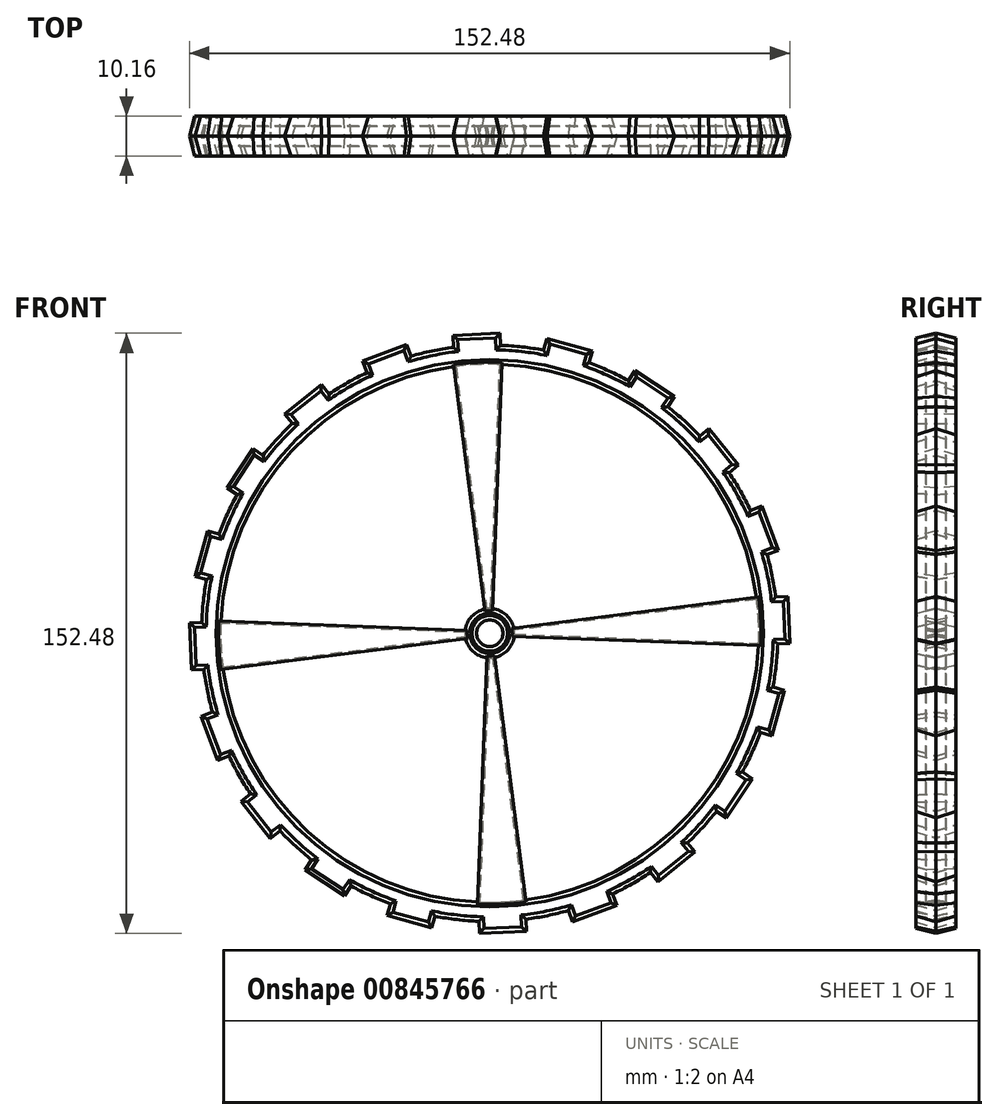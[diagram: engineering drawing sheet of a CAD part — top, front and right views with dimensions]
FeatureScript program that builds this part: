
annotation { "Feature Type Name" : "Feature", "Feature Type Description" : "" }
export const myFeature = defineFeature(function(context is Context, id is Id, definition is map)
    precondition{}
    {
        {
            var Q0;
            Q0=qCreatedBy(makeId("Front.planeOp"),FACE);
            var sketch = newSketch(context, id + "F0", { "sketchPlane" : qUnion([Q0])});
            skArc(sketch, "E0.cCircle", {"start": v(2.62, 76) * mm, "mid": v(-3.37, 75.98) * mm, "end": v(-9.34, 75.47) * mm, "construction": true});
            skLineSegment(sketch, "E0.3", {"start": v(75.71, 9.35) * mm, "end": v(76.24, -2.6) * mm});
            skLineSegment(sketch, "E0.5", {"start": v(73.3, -20.27) * mm, "end": v(71.7, -26.04) * mm});
            skLineSegment(sketch, "E0.7", {"start": v(66.75, -36.93) * mm, "end": v(60.15, -46.92) * mm});
            skLineSegment(sketch, "E0.9", {"start": v(52.07, -55.75) * mm, "end": v(47.39, -59.48) * mm});
            skLineSegment(sketch, "E0.11", {"start": v(32.3, -69.11) * mm, "end": v(21.08, -73.32) * mm});
            skLineSegment(sketch, "E0.13", {"start": v(9.35, -75.71) * mm, "end": v(-2.6, -76.24) * mm});
            skLineSegment(sketch, "E0.17", {"start": v(-36.93, -66.75) * mm, "end": v(-46.92, -60.15) * mm});
            skLineSegment(sketch, "E0.23", {"start": v(-75.71, -9.35) * mm, "end": v(-76.24, 2.6) * mm});
            skLineSegment(sketch, "E0.25", {"start": v(-74.9, 14.5) * mm, "end": v(-71.7, 26.04) * mm});
            skLineSegment(sketch, "E0.27", {"start": v(-66.75, 36.93) * mm, "end": v(-60.15, 46.92) * mm});
            skLineSegment(sketch, "E0.29", {"start": v(-52.07, 55.75) * mm, "end": v(-42.7, 63.21) * mm});
            skLineSegment(sketch, "E0.31", {"start": v(-32.3, 69.11) * mm, "end": v(-21.08, 73.32) * mm});
            skLineSegment(sketch, "E0.33", {"start": v(-9.35, 75.71) * mm, "end": v(2.6, 76.24) * mm});
            skLineSegment(sketch, "E0.35", {"start": v(14.5, 74.9) * mm, "end": v(26.04, 71.7) * mm});
            skLineSegment(sketch, "E0.37", {"start": v(36.93, 66.75) * mm, "end": v(46.92, 60.15) * mm});
            skLineSegment(sketch, "E0.39", {"start": v(55.75, 52.07) * mm, "end": v(63.21, 42.7) * mm});
            skPoint(sketch, "E0.0.midPoint", {"position": v(66.16, 37.5) * mm});
            skLineSegment(sketch, "E1", {"start": v(-9.35, 75.71) * mm, "end": v(-9.22, 72.64) * mm});
            skLineSegment(sketch, "E2", {"start": v(2.6, 76.24) * mm, "end": v(2.74, 73.17) * mm});
            skLineSegment(sketch, "E3", {"start": v(14.5, 74.9) * mm, "end": v(13.68, 71.93) * mm});
            skLineSegment(sketch, "E4", {"start": v(26.04, 71.7) * mm, "end": v(25.22, 68.74) * mm});
            skLineSegment(sketch, "E5", {"start": v(36.93, 66.75) * mm, "end": v(35.24, 64.18) * mm});
            skLineSegment(sketch, "E6", {"start": v(-36.93, -66.75) * mm, "end": v(-35.24, -64.18) * mm});
            skLineSegment(sketch, "E7", {"start": v(55.75, 52.07) * mm, "end": v(53.35, 50.15) * mm});
            skLineSegment(sketch, "E8", {"start": v(-55.75, -52.07) * mm, "end": v(-55.57, -51.92) * mm});
            skLineSegment(sketch, "E9", {"start": v(69.11, 32.3) * mm, "end": v(66.23, 31.21) * mm});
            skLineSegment(sketch, "E10", {"start": v(-69.11, -32.3) * mm, "end": v(-66.23, -31.21) * mm});
            skLineSegment(sketch, "E11", {"start": v(75.71, 9.35) * mm, "end": v(72.64, 9.22) * mm});
            skLineSegment(sketch, "E12", {"start": v(-75.71, -9.35) * mm, "end": v(-72.64, -9.22) * mm});
            skLineSegment(sketch, "E13", {"start": v(74.9, -14.5) * mm, "end": v(71.93, -13.68) * mm});
            skLineSegment(sketch, "E14", {"start": v(-74.9, 14.5) * mm, "end": v(-71.93, 13.68) * mm});
            skLineSegment(sketch, "E15", {"start": v(66.75, -36.93) * mm, "end": v(64.18, -35.24) * mm});
            skLineSegment(sketch, "E16", {"start": v(-66.75, 36.93) * mm, "end": v(-64.18, 35.24) * mm});
            skLineSegment(sketch, "E17", {"start": v(52.1, -55.6) * mm, "end": v(50.24, -53.27) * mm});
            skLineSegment(sketch, "E18", {"start": v(-52.07, 55.75) * mm, "end": v(-50.15, 53.35) * mm});
            skLineSegment(sketch, "E19", {"start": v(32.3, -69.11) * mm, "end": v(31.21, -66.23) * mm});
            skLineSegment(sketch, "E20", {"start": v(-32.3, 69.11) * mm, "end": v(-31.21, 66.23) * mm});
            skArc(sketch, "E21.trimOffspring", {"start": v(25.98, 71.48) * mm, "mid": v(20.27, 73.3) * mm, "end": v(14.44, 74.67) * mm, "construction": true});
            skArc(sketch, "E22.trimOffspring", {"start": v(46.8, 59.95) * mm, "mid": v(41.93, 63.45) * mm, "end": v(36.8, 66.55) * mm, "construction": true});
            skArc(sketch, "E23.trimOffspring", {"start": v(63.03, 42.56) * mm, "mid": v(59.48, 47.39) * mm, "end": v(55.57, 51.92) * mm, "construction": true});
            skArc(sketch, "E24.trimOffspring", {"start": v(73.1, 21) * mm, "mid": v(71.21, 26.69) * mm, "end": v(68.9, 32.2) * mm, "construction": true});
            skArc(sketch, "E25.trimOffspring", {"start": v(76, -2.62) * mm, "mid": v(75.98, 3.37) * mm, "end": v(75.47, 9.34) * mm, "construction": true});
            skArc(sketch, "E26.trimOffspring", {"start": v(71.48, -25.98) * mm, "mid": v(73.3, -20.27) * mm, "end": v(74.67, -14.44) * mm, "construction": true});
            skArc(sketch, "E27.trimOffspring", {"start": v(21, -73.1) * mm, "mid": v(26.69, -71.21) * mm, "end": v(32.2, -68.9) * mm, "construction": true});
            skArc(sketch, "E28.trimOffspring", {"start": v(42.56, -63.03) * mm, "mid": v(47.43, -59.45) * mm, "end": v(52, -55.49) * mm, "construction": true});
            skArc(sketch, "E29.trimOffspring", {"start": v(59.95, -46.8) * mm, "mid": v(63.45, -41.93) * mm, "end": v(66.55, -36.8) * mm, "construction": true});
            skArc(sketch, "E30.trimOffspring", {"start": v(-2.62, -76) * mm, "mid": v(0.38, -76.05) * mm, "end": v(3.37, -75.98) * mm, "construction": true});
            skArc(sketch, "E31.trimOffspring", {"start": v(-25.98, -71.48) * mm, "mid": v(-20.4, -73.26) * mm, "end": v(-14.71, -74.61) * mm, "construction": true});
            skArc(sketch, "E32.trimOffspring", {"start": v(-46.8, -59.95) * mm, "mid": v(-41.93, -63.45) * mm, "end": v(-36.8, -66.55) * mm, "construction": true});
            skArc(sketch, "E33.trimOffspring", {"start": v(-63.03, -42.56) * mm, "mid": v(-59.48, -47.39) * mm, "end": v(-55.57, -51.92) * mm, "construction": true});
            skArc(sketch, "E34.trimOffspring", {"start": v(-73.1, -21) * mm, "mid": v(-71.21, -26.69) * mm, "end": v(-68.9, -32.2) * mm, "construction": true});
            skArc(sketch, "E35.trimOffspring", {"start": v(-76, 2.62) * mm, "mid": v(-75.98, -3.37) * mm, "end": v(-75.47, -9.34) * mm, "construction": true});
            skArc(sketch, "E36.trimOffspring", {"start": v(-71.48, 25.98) * mm, "mid": v(-73.3, 20.27) * mm, "end": v(-74.67, 14.44) * mm, "construction": true});
            skArc(sketch, "E37.trimOffspring", {"start": v(-59.95, 46.8) * mm, "mid": v(-63.45, 41.93) * mm, "end": v(-66.55, 36.8) * mm, "construction": true});
            skArc(sketch, "E38.trimOffspring", {"start": v(-42.56, 63.03) * mm, "mid": v(-47.39, 59.48) * mm, "end": v(-51.92, 55.57) * mm, "construction": true});
            skArc(sketch, "E39.trimOffspring", {"start": v(-21, 73.1) * mm, "mid": v(-26.69, 71.21) * mm, "end": v(-32.2, 68.9) * mm, "construction": true});
            skLineSegment(sketch, "E40.trimOffspring", {"start": v(-20, 70.43) * mm, "end": v(-21.08, 73.32) * mm});
            skLineSegment(sketch, "E41.trimOffspring", {"start": v(45.22, 57.58) * mm, "end": v(46.92, 60.15) * mm});
            skLineSegment(sketch, "E42.trimOffspring", {"start": v(60.8, 40.79) * mm, "end": v(63.21, 42.7) * mm});
            skLineSegment(sketch, "E43.trimOffspring", {"start": v(70.43, 20) * mm, "end": v(73.32, 21.08) * mm});
            skLineSegment(sketch, "E44.trimOffspring", {"start": v(73.17, -2.74) * mm, "end": v(76.24, -2.6) * mm});
            skLineSegment(sketch, "E45.trimOffspring", {"start": v(68.74, -25.22) * mm, "end": v(71.7, -26.04) * mm});
            skLineSegment(sketch, "E46.trimOffspring", {"start": v(57.58, -45.22) * mm, "end": v(60.15, -46.92) * mm});
            skLineSegment(sketch, "E47.trimOffspring", {"start": v(40.79, -60.8) * mm, "end": v(42.7, -63.21) * mm});
            skLineSegment(sketch, "E48.trimOffspring", {"start": v(9.22, -72.64) * mm, "end": v(9.35, -75.71) * mm});
            skLineSegment(sketch, "E49.trimOffspring", {"start": v(20, -70.43) * mm, "end": v(21.08, -73.32) * mm});
            skLineSegment(sketch, "E50.trimOffspring", {"start": v(-2.74, -73.17) * mm, "end": v(-2.6, -76.24) * mm});
            skLineSegment(sketch, "E51.trimOffspring", {"start": v(-25.22, -68.74) * mm, "end": v(-26.04, -71.7) * mm});
            skLineSegment(sketch, "E52.trimOffspring", {"start": v(-45.22, -57.58) * mm, "end": v(-46.92, -60.15) * mm});
            skLineSegment(sketch, "E53.trimOffspring", {"start": v(-60.8, -40.79) * mm, "end": v(-63.21, -42.7) * mm});
            skLineSegment(sketch, "E54.trimOffspring", {"start": v(-70.43, -20) * mm, "end": v(-73.32, -21.08) * mm});
            skLineSegment(sketch, "E55.trimOffspring", {"start": v(-73.17, 2.74) * mm, "end": v(-76.24, 2.6) * mm});
            skLineSegment(sketch, "E56.trimOffspring", {"start": v(-68.74, 25.22) * mm, "end": v(-71.7, 26.04) * mm});
            skLineSegment(sketch, "E57.trimOffspring", {"start": v(-40.79, 60.8) * mm, "end": v(-42.7, 63.21) * mm});
            skLineSegment(sketch, "E58.trimOffspring", {"start": v(-57.58, 45.22) * mm, "end": v(-60.15, 46.92) * mm});
            skCircle(sketch, "E59", {"center": v(0, 0) * mm, "radius": 73.22 * mm});
            skLineSegment(sketch, "E60", {"start": v(-14.77, -74.8) * mm, "end": v(-13.94, -71.88) * mm});
            skLineSegment(sketch, "E61", {"start": v(42.7, -63.21) * mm, "end": v(52.1, -55.6) * mm});
            skLineSegment(sketch, "E62", {"start": v(74.9, -14.5) * mm, "end": v(71.7, -26.04) * mm});
            skCircle(sketch, "E63", {"center": v(0, 0) * mm, "radius": 6.26 * mm});
            skCircle(sketch, "E64", {"center": v(0, 0) * mm, "radius": 68.37 * mm});
            skLineSegment(sketch, "E65", {"start": v(-8.6, 67.83) * mm, "end": v(-0.79, 6.21) * mm});
            skLineSegment(sketch, "E66", {"start": v(2.56, 68.32) * mm, "end": v(0.23, 6.26) * mm});
            skLineSegment(sketch, "E67", {"start": v(67.83, 8.6) * mm, "end": v(6.21, 0.79) * mm});
            skLineSegment(sketch, "E68", {"start": v(6.26, -0.23) * mm, "end": v(68.32, -2.56) * mm});
            skLineSegment(sketch, "E69", {"start": v(0.79, -6.21) * mm, "end": v(8.6, -67.83) * mm});
            skLineSegment(sketch, "E70", {"start": v(-0.23, -6.26) * mm, "end": v(-2.56, -68.32) * mm});
            skLineSegment(sketch, "E71", {"start": v(-67.83, -8.6) * mm, "end": v(-6.21, -0.79) * mm});
            skLineSegment(sketch, "E72", {"start": v(-68.32, 2.56) * mm, "end": v(-6.26, 0.23) * mm});
            skLineSegment(sketch, "E73", {"start": v(69.11, 32.3) * mm, "end": v(73.32, 21.08) * mm});
            skLineSegment(sketch, "E74", {"start": v(-26.04, -71.7) * mm, "end": v(-14.77, -74.8) * mm});
            skLineSegment(sketch, "E75", {"start": v(-53.3, -50.2) * mm, "end": v(-55.57, -51.92) * mm});
            skLineSegment(sketch, "E76", {"start": v(-63.21, -42.7) * mm, "end": v(-55.75, -52.07) * mm});
            skLineSegment(sketch, "E77", {"start": v(-73.32, -21.08) * mm, "end": v(-69.11, -32.3) * mm});
            skCircle(sketch, "E78", {"center": v(0, 0) * mm, "radius": 3.36 * mm});
            skCircle(sketch, "E79.0", {"center": v(0, 0) * mm, "radius": 1.55 * mm});
            skSolve(sketch);
        }
        {
            var Q0;
            Q0=makeQuery(id+"F0.imprint","IMPRINT",FACE,{"disambiguationData":[TD([[makeQuery(id+"F0.imprint","IMPRINT",EDGE,{"derivedFrom":sQuery(id+"F0.wireOp",EDGE,"E0.35")}),-1.0]])]});
            var Q1;
            Q1=makeQuery(id+"F0.imprint","IMPRINT",FACE,{"disambiguationData":[TD([[makeQuery(id+"F0.imprint","IMPRINT",EDGE,{"derivedFrom":sQuery(id+"F0.wireOp",EDGE,"E0.37")}),-1.0]])]});
            var Q2;
            Q2=makeQuery(id+"F0.imprint","IMPRINT",FACE,{"disambiguationData":[TD([[makeQuery(id+"F0.imprint","IMPRINT",EDGE,{"derivedFrom":sQuery(id+"F0.wireOp",EDGE,"E0.33")}),-1.0]])]});
            var Q3;
            Q3=makeQuery(id+"F0.imprint","IMPRINT",FACE,{"disambiguationData":[TD([[makeQuery(id+"F0.imprint","IMPRINT",EDGE,{"derivedFrom":sQuery(id+"F0.wireOp",EDGE,"E0.31")}),-1.0]])]});
            var Q4;
            Q4=makeQuery(id+"F0.imprint","IMPRINT",FACE,{"disambiguationData":[TD([[makeQuery(id+"F0.imprint","IMPRINT",EDGE,{"derivedFrom":sQuery(id+"F0.wireOp",EDGE,"E0.29")}),-1.0]])]});
            var Q5;
            Q5=makeQuery(id+"F0.imprint","IMPRINT",FACE,{"disambiguationData":[TD([[makeQuery(id+"F0.imprint","IMPRINT",EDGE,{"derivedFrom":sQuery(id+"F0.wireOp",EDGE,"E0.27")}),-1.0]])]});
            var Q6;
            Q6=makeQuery(id+"F0.imprint","IMPRINT",FACE,{"disambiguationData":[TD([[makeQuery(id+"F0.imprint","IMPRINT",EDGE,{"derivedFrom":sQuery(id+"F0.wireOp",EDGE,"E0.25")}),-1.0]])]});
            var Q7;
            Q7=makeQuery(id+"F0.imprint","IMPRINT",FACE,{"disambiguationData":[TD([[makeQuery(id+"F0.imprint","IMPRINT",EDGE,{"derivedFrom":sQuery(id+"F0.wireOp",EDGE,"E0.23")}),-1.0]])]});
            var Q8;
            {var subQ0=sQuery(id+"F0.wireOp",EDGE,"E10");Q8=makeQuery(id+"F0.imprint","IMPRINT",FACE,{"disambiguationData":[TD([[makeQuery(id+"F0.imprint","IMPRINT",EDGE,{"derivedFrom":subQ0}),1.0]])]});}
            var Q9;
            Q9=makeQuery(id+"F0.imprint","IMPRINT",FACE,{"disambiguationData":[TD([[makeQuery(id+"F0.imprint","IMPRINT",EDGE,{"derivedFrom":sQuery(id+"F0.wireOp",EDGE,"E8")}),1.0]])]});
            var Q10;
            {var subQ0=sQuery(id+"F0.wireOp",EDGE,"E59");var subQ1=makeQuery(id+"F0.imprint","INTERSECT",VERTEX,{"derivedFrom":[sQuery(id+"F0.wireOp",EDGE,"E11"),subQ0]});Q10=makeQuery(id+"F0.imprint","IMPRINT",FACE,{"disambiguationData":[TD([[makeQuery(id+"F0.imprint","IMPRINT",EDGE,{"disambiguationData":[TD([[subQ1,-1.0]])],"derivedFrom":subQ0}),1.0]])]});}
            var Q11;
            Q11=makeQuery(id+"F0.imprint","IMPRINT",FACE,{"disambiguationData":[TD([[makeQuery(id+"F0.imprint","IMPRINT",EDGE,{"derivedFrom":sQuery(id+"F0.wireOp",EDGE,"E0.17")}),-1.0]])]});
            var Q12;
            {var subQ0=sQuery(id+"F0.wireOp",EDGE,"E51.trimOffspring");Q12=makeQuery(id+"F0.imprint","IMPRINT",FACE,{"disambiguationData":[TD([[makeQuery(id+"F0.imprint","IMPRINT",EDGE,{"derivedFrom":subQ0}),1.0]])]});}
            var Q13;
            Q13=makeQuery(id+"F0.imprint","IMPRINT",FACE,{"disambiguationData":[TD([[makeQuery(id+"F0.imprint","IMPRINT",EDGE,{"derivedFrom":sQuery(id+"F0.wireOp",EDGE,"E0.13")}),-1.0]])]});
            var Q14;
            Q14=makeQuery(id+"F0.imprint","IMPRINT",FACE,{"disambiguationData":[TD([[makeQuery(id+"F0.imprint","IMPRINT",EDGE,{"derivedFrom":sQuery(id+"F0.wireOp",EDGE,"E0.11")}),-1.0]])]});
            var Q15;
            {var subQ0=sQuery(id+"F0.wireOp",EDGE,"E17");Q15=makeQuery(id+"F0.imprint","IMPRINT",FACE,{"disambiguationData":[TD([[makeQuery(id+"F0.imprint","IMPRINT",EDGE,{"derivedFrom":subQ0}),1.0]])]});}
            var Q16;
            Q16=makeQuery(id+"F0.imprint","IMPRINT",FACE,{"disambiguationData":[TD([[makeQuery(id+"F0.imprint","IMPRINT",EDGE,{"derivedFrom":sQuery(id+"F0.wireOp",EDGE,"E0.7")}),-1.0]])]});
            var Q17;
            {var subQ0=sQuery(id+"F0.wireOp",EDGE,"E13");Q17=makeQuery(id+"F0.imprint","IMPRINT",FACE,{"disambiguationData":[TD([[makeQuery(id+"F0.imprint","IMPRINT",EDGE,{"derivedFrom":subQ0}),1.0]])]});}
            var Q18;
            Q18=makeQuery(id+"F0.imprint","IMPRINT",FACE,{"disambiguationData":[TD([[makeQuery(id+"F0.imprint","IMPRINT",EDGE,{"derivedFrom":sQuery(id+"F0.wireOp",EDGE,"E0.3")}),-1.0]])]});
            var Q19;
            {var subQ0=sQuery(id+"F0.wireOp",EDGE,"E9");Q19=makeQuery(id+"F0.imprint","IMPRINT",FACE,{"disambiguationData":[TD([[makeQuery(id+"F0.imprint","IMPRINT",EDGE,{"derivedFrom":subQ0}),1.0]])]});}
            var Q20;
            Q20=makeQuery(id+"F0.imprint","IMPRINT",FACE,{"disambiguationData":[TD([[makeQuery(id+"F0.imprint","IMPRINT",EDGE,{"derivedFrom":sQuery(id+"F0.wireOp",EDGE,"E0.39")}),-1.0]])]});
            var Q21;
            Q21=makeQuery(id+"F0.imprint","IMPRINT",FACE,{"disambiguationData":[TD([[makeQuery(id+"F0.imprint","IMPRINT",EDGE,{"derivedFrom":sQuery(id+"F0.wireOp",EDGE,"E78")}),-1.0]])]});
            extrude(context, id + "F1", {"entities" : qUnion([Q0, Q1, Q2, Q3, Q4, Q5, Q6, Q7, Q8, Q9, Q10, Q11, Q12, Q13, Q14, Q15, Q16, Q17, Q18, Q19, Q20, Q21]), "endBound" : BoundingType.SYMMETRIC, "depth" : 10.16 * mm, "offsetDistance" : 25.4 * mm, "hasDraft" : true, "draftAngle" : 13 * degree, "draftPullDirection" : true});
        }
        {
            var Q0;
            {var subQ0=sQuery(id+"F0.wireOp",EDGE,"E69");Q0=makeQuery(id+"F0.imprint","IMPRINT",FACE,{"disambiguationData":[TD([[makeQuery(id+"F0.imprint","IMPRINT",EDGE,{"derivedFrom":subQ0}),-1.0]])]});}
            var Q1;
            {var subQ0=sQuery(id+"F0.wireOp",EDGE,"E71");Q1=makeQuery(id+"F0.imprint","IMPRINT",FACE,{"disambiguationData":[TD([[makeQuery(id+"F0.imprint","IMPRINT",EDGE,{"derivedFrom":subQ0}),1.0]])]});}
            var Q2;
            {var subQ0=sQuery(id+"F0.wireOp",EDGE,"E65");Q2=makeQuery(id+"F0.imprint","IMPRINT",FACE,{"disambiguationData":[TD([[makeQuery(id+"F0.imprint","IMPRINT",EDGE,{"derivedFrom":subQ0}),1.0]])]});}
            var Q3;
            {var subQ0=sQuery(id+"F0.wireOp",EDGE,"E67");Q3=makeQuery(id+"F0.imprint","IMPRINT",FACE,{"disambiguationData":[TD([[makeQuery(id+"F0.imprint","IMPRINT",EDGE,{"derivedFrom":subQ0}),1.0]])]});}
            extrude(context, id + "F2", {"entities" : qUnion([Q0, Q1, Q2, Q3]), "operationType" : NewBodyOperationType.ADD, "endBound" : BoundingType.SYMMETRIC, "oppositeDirection" : true, "depth" : 5.08 * mm, "offsetDistance" : 25.4 * mm, "hasDraft" : true, "draftAngle" : 12 * degree});
        }
    });
